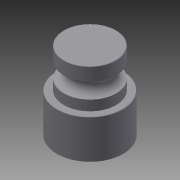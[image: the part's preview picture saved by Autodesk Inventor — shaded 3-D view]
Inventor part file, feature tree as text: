
AUTODESK INVENTOR PART (.ipt)
format: ipt  version: 2013 (Build 170138000, 138)  size: 129,536 bytes
history: native  units: mm
features: chamfer x2, sketch x2, revolve x1, extrude x1
ambient origin geometry x8: Origin, YZ Plane, XZ Plane, XY Plane, X Axis, Y Axis, Z Axis, Center Point
bodies: Solid1 (feature_tree)
feature tree (6):
  revolve  "Revolution1"  [1 undecoded]
  chamfer  "Chamfer1"  Distance=13.45mm
  extrude  "Extrusion1"  Depth=8.0mm
  chamfer  "Chamfer2"  Distance=4.0mm
  sketch  "Sketch1"  dims[d0=20.0mm d1=13.45mm]
  sketch  "Sketch2"  dims[d2=6.8mm d3=13.45mm d4=8.0mm d5=4.0mm d6=90.0deg d7=0.2mm d8=2.0mm d9=45.0deg d10=34.0mm d11=20.0mm d12=0.0mm d13=0.2mm d14=2.0mm d15=45.0deg]
note: 1 required parameter value undecoded (feature->parameter linkage not recoverable at this tier; creation-order binding heuristic only, values carry confidence <= 0.55)
